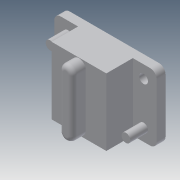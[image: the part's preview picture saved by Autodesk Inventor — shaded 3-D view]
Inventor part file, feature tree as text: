
AUTODESK INVENTOR PART (.ipt)
format: ipt  version: 2014 (Build 180170000, 170)  size: 139,776 bytes
history: native  units: in
note: dims shown in document units (in); Inventor stores cm internally (conversion verified against a paired STEP export)
features: extrude x4, sketch x4, fillet x1, projected_geometry x1
ambient origin geometry x8: Origin, YZ Plane, XZ Plane, XY Plane, X Axis, Y Axis, Z Axis, Center Point
bodies: Solid1 (feature_tree)
feature tree (10):
  extrude  "Extrusion1"  Depth=1.9in
  extrude  "Extrusion2"  Depth=0.25in
  extrude  "Extrusion3"  Depth=0.25in TaperAngle=0.0deg
  fillet  "Fillet1"  Radius=1.55in
  extrude  "Extrusion4"  Depth=0.375in TaperAngle=0.0deg
  sketch  "Sketch1"  dims[d0=2.9in d1=1.9in]
  sketch  "Sketch2"  dims[d2=0.1875in d3=0.25in]
  sketch  "Sketch3"  dims[d4=0.25in d5=0.25in d6=0.0in d7=1.55in]
  sketch  "Sketch4"  dims[d8=0.75in d9=0.0in d10=0.375in d11=0.0in d12=0.125in d13=0.5in d14=0.0in]
  projected_geometry  "Projected Loop1"
